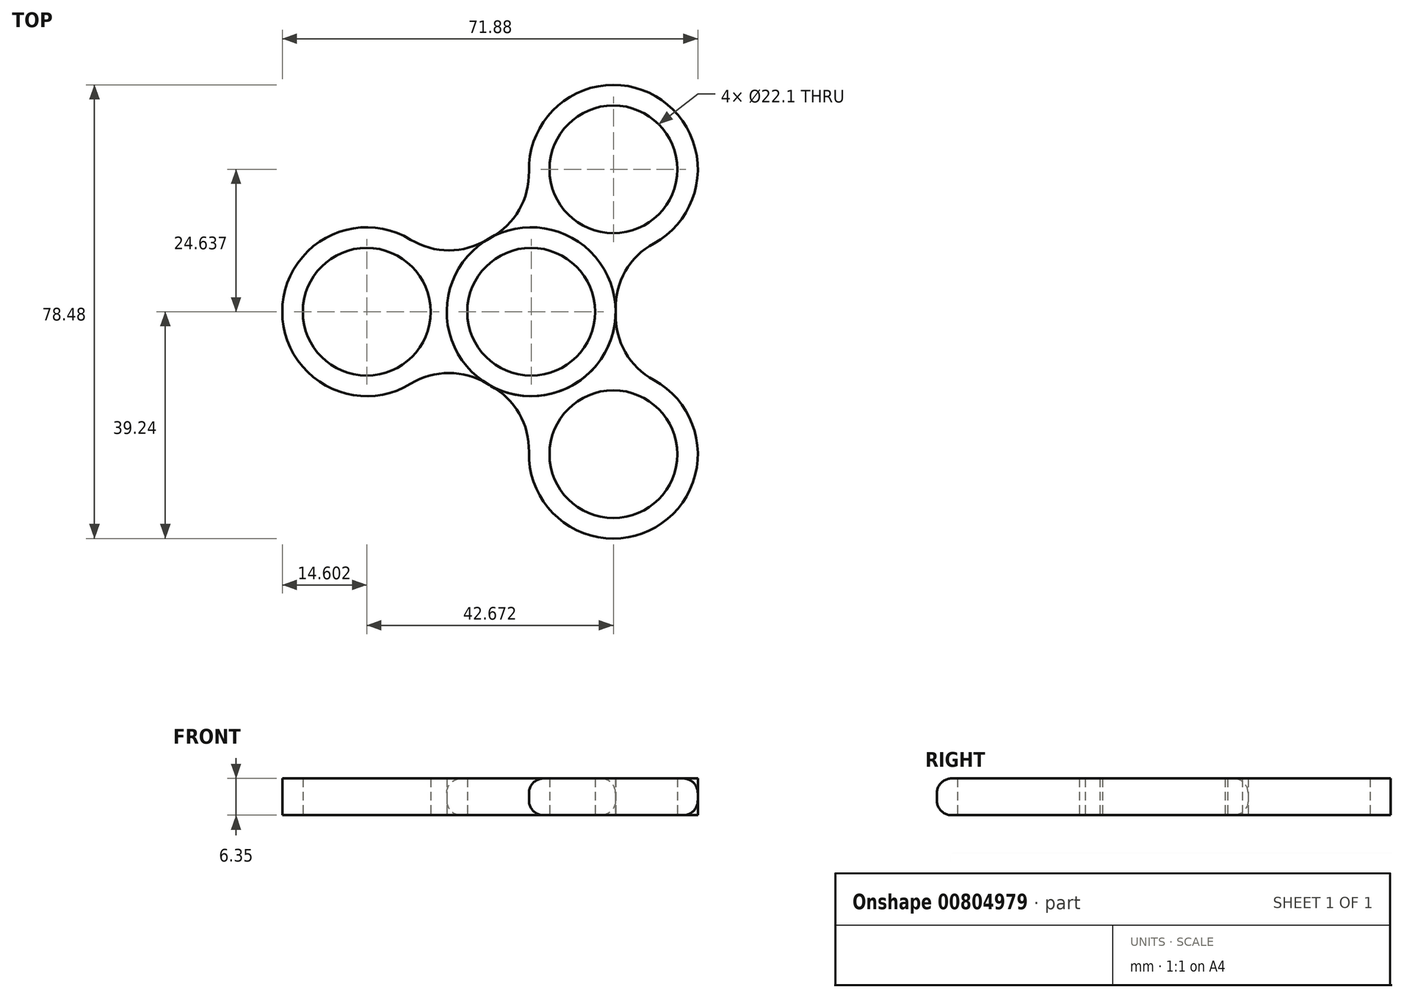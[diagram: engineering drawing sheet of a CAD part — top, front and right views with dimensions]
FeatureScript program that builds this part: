
annotation { "Feature Type Name" : "Feature", "Feature Type Description" : "" }
export const myFeature = defineFeature(function(context is Context, id is Id, definition is map)
    precondition{}
    {
        {
            var Q0;
            Q0=qCreatedBy(makeId("Top.planeOp"),FACE);
            var sketch = newSketch(context, id + "F0", { "sketchPlane" : qUnion([Q0])});
            skCircle(sketch, "E0", {"center": v(0, 0) * mm, "radius": 11.05 * mm});
            skArc(sketch, "E1", {"start": v(-7.6, -12.47) * mm, "mid": v(14.6, 0) * mm, "end": v(-7.6, 12.47) * mm});
            skCircle(sketch, "E2", {"center": v(-28.45, 0) * mm, "radius": 11.05 * mm});
            skArc(sketch, "E3", {"start": v(-20.84, 12.47) * mm, "mid": v(-43.05, 0) * mm, "end": v(-20.84, -12.47) * mm});
            skArc(sketch, "E4", {"start": v(-7.6, -12.47) * mm, "mid": v(-14.22, -10.6) * mm, "end": v(-20.84, -12.47) * mm});
            skArc(sketch, "E5", {"start": v(-20.84, 12.47) * mm, "mid": v(-14.22, 10.6) * mm, "end": v(-7.6, 12.47) * mm});
            skSolve(sketch);
        }
        {
            var Q0;
            Q0=makeQuery(id+"F0.imprint","IMPRINT",FACE,{"disambiguationData":[TD([[makeQuery(id+"F0.imprint","IMPRINT",EDGE,{"derivedFrom":sQuery(id+"F0.wireOp",EDGE,"E0")}),-1.0]])]});
            extrude(context, id + "F1", {"entities" : qUnion([Q0]), "depth" : 6.35 * mm, "offsetDistance" : 25.4 * mm});
        }
        {
            var Q0;
            Q0=qCreatedBy(makeId("Right.planeOp"),FACE);
            var sketch = newSketch(context, id + "F2", { "sketchPlane" : qUnion([Q0])});
            skLineSegment(sketch, "E6", {"start": v(0, 0) * mm, "end": v(0, 18.42) * mm});
            skSolve(sketch);
        }
        {
            var Q0;
            Q0=makeQuery(id+"F1.opExtrude","SWEPT_BODY",BODY,{"disambiguationData":[OSD([sQuery(id+"F0.wireOp",EDGE,"E0"),sQuery(id+"F0.wireOp",EDGE,"E1"),sQuery(id+"F0.wireOp",EDGE,"E2"),sQuery(id+"F0.wireOp",EDGE,"E3"),sQuery(id+"F0.wireOp",EDGE,"E4"),sQuery(id+"F0.wireOp",EDGE,"E5")])]});
            var Q1;
            Q1=sQuery(id+"F2.wireOp",EDGE,"E6");
            circularPattern(context, id + "F3", {"entities" : qUnion([Q0]), "axis" : qUnion([Q1]), "angle" : 360 * degree, "instanceCount" : 3, "equalSpace" : true});
        }
        {
            var Q0;
            Q0=makeQuery(id+"F3.opPattern","COPY",EDGE,{"derivedFrom":makeQuery(id+"F1.opExtrude","CAP_EDGE",EDGE,{"disambiguationData":[OSD([sQuery(id+"F0.wireOp",EDGE,"E5")])],"isStart":false}),"instanceName":"1"});
            var Q1;
            Q1=makeQuery(id+"F3.opPattern","COPY",EDGE,{"derivedFrom":makeQuery(id+"F1.opExtrude","CAP_EDGE",EDGE,{"disambiguationData":[OSD([sQuery(id+"F0.wireOp",EDGE,"E5")])],"isStart":true}),"instanceName":"1"});
            fillet(context, id + "F4", {"entities" : qUnion([Q0, Q1]), "radius" : 2.54 * mm, "tangentPropagation" : true, "allowEdgeOverflow" : false});
        }
    });
